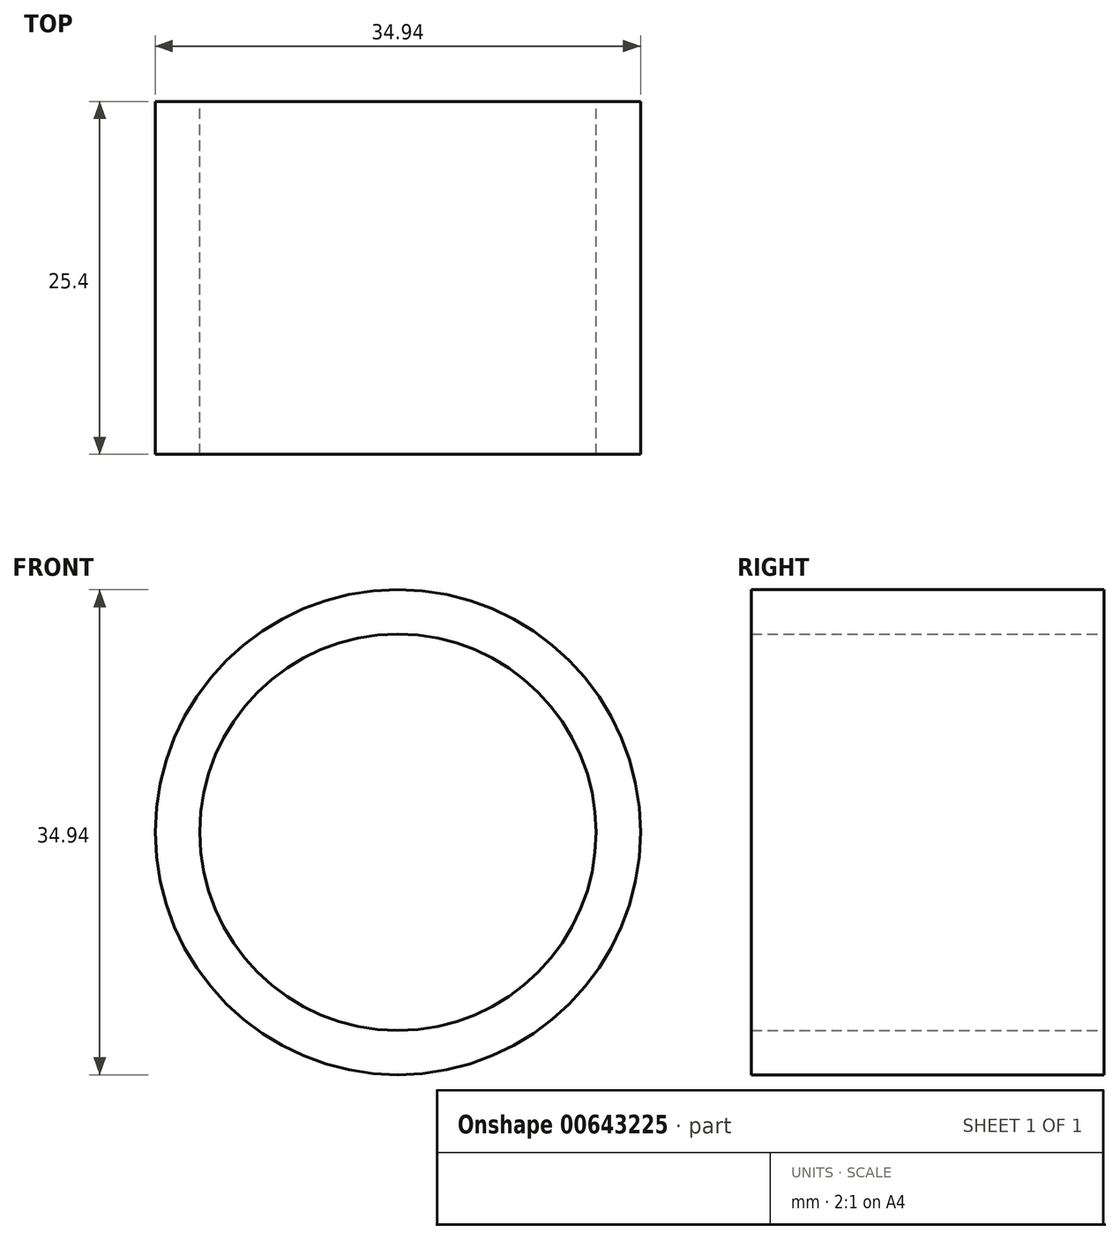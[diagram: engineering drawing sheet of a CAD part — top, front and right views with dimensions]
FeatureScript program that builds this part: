
annotation { "Feature Type Name" : "Feature", "Feature Type Description" : "" }
export const myFeature = defineFeature(function(context is Context, id is Id, definition is map)
    precondition{}
    {
        {
            var Q0;
            Q0=qCreatedBy(makeId("Front.planeOp"),FACE);
            var sketch = newSketch(context, id + "F0", { "sketchPlane" : qUnion([Q0])});
            skCircle(sketch, "E0", {"center": v(-56.2, 46.06) * mm, "radius": 17.47 * mm});
            skCircle(sketch, "E1", {"center": v(-56.2, 46.06) * mm, "radius": 14.27 * mm});
            skSolve(sketch);
        }
        {
            var Q0;
            Q0=makeQuery(id+"F0.imprint","IMPRINT",FACE,{"disambiguationData":[TD([[makeQuery(id+"F0.imprint","IMPRINT",EDGE,{"derivedFrom":sQuery(id+"F0.wireOp",EDGE,"E0")}),1.0]])]});
            extrude(context, id + "F1", {"entities" : qUnion([Q0]), "depth" : 25.4 * mm, "offsetDistance" : 25.4 * mm});
        }
    });
